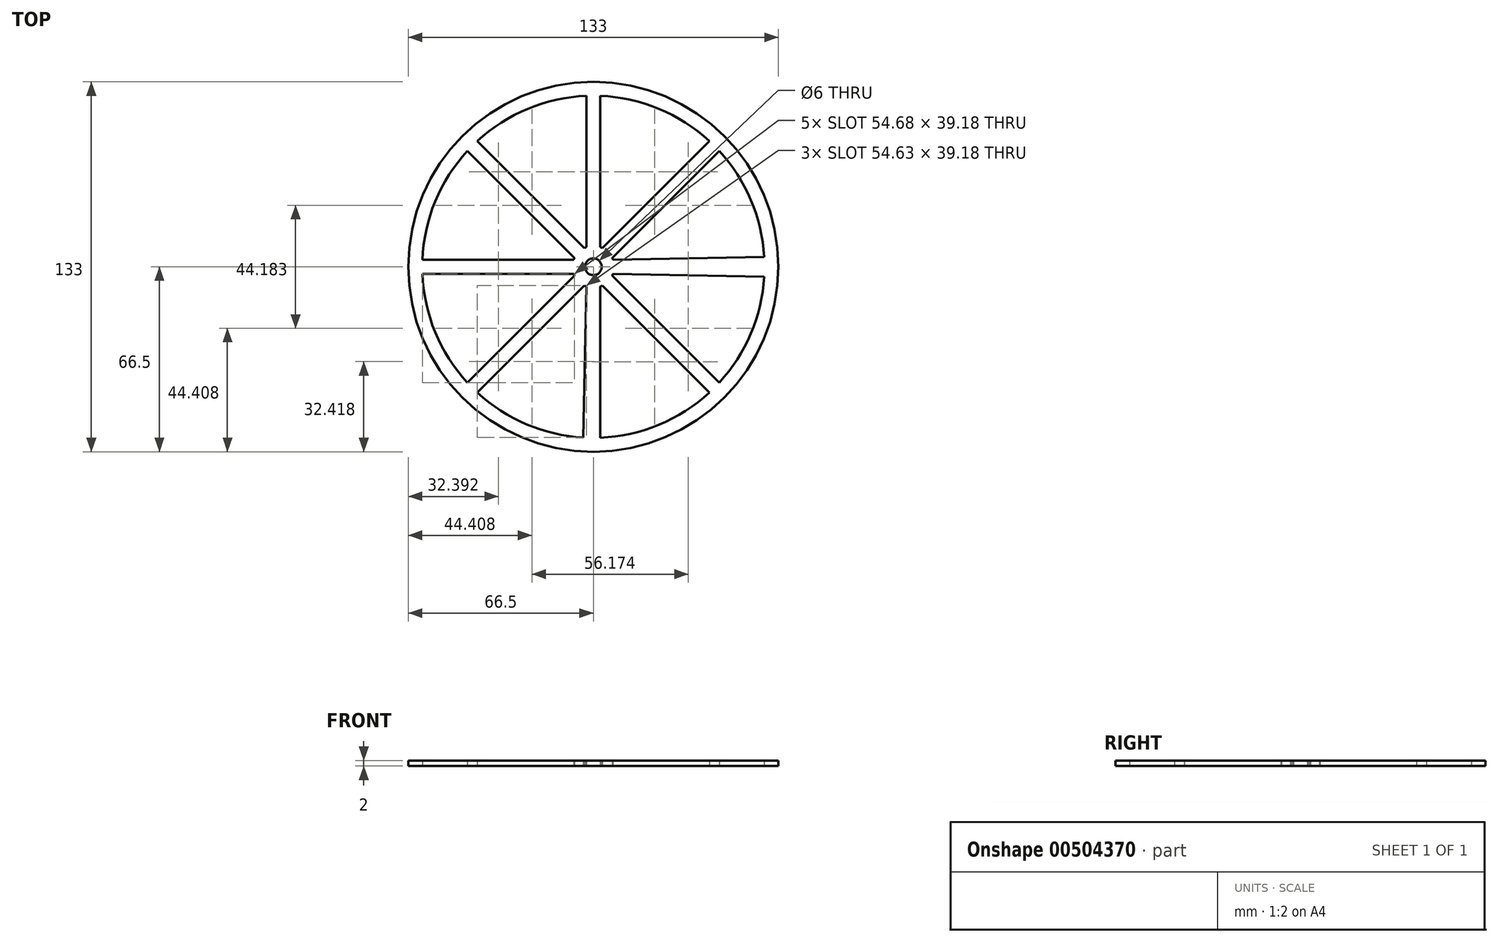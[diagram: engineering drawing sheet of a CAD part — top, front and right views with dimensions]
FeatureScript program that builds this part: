
annotation { "Feature Type Name" : "Feature", "Feature Type Description" : "" }
export const myFeature = defineFeature(function(context is Context, id is Id, definition is map)
    precondition{}
    {
        {
            var Q0;
            Q0=qCreatedBy(makeId("Top.planeOp"),FACE);
            var sketch = newSketch(context, id + "F0", { "sketchPlane" : qUnion([Q0])});
            skArc(sketch, "E0", {"start": v(-45.22, 41.68) * mm, "mid": v(-56.82, 23.54) * mm, "end": v(-61.45, 2.5) * mm});
            skCircle(sketch, "E1", {"center": v(0, 0) * mm, "radius": 66.5 * mm});
            skLineSegment(sketch, "E2", {"start": v(0, 0) * mm, "end": v(-41.68, 41.68) * mm, "construction": true});
            skLineSegment(sketch, "E3.left", {"start": v(-2.5, 61.45) * mm, "end": v(-2.5, 7.07) * mm});
            skLineSegment(sketch, "E3.right", {"start": v(2.5, 42.93) * mm, "end": v(2.5, 7.07) * mm});
            skLineSegment(sketch, "E4.bottom", {"start": v(-61.45, 2.5) * mm, "end": v(-7.07, 2.5) * mm});
            skLineSegment(sketch, "E4.top", {"start": v(-61.45, -2.5) * mm, "end": v(-7.07, -2.5) * mm});
            skLineSegment(sketch, "E5", {"start": v(-41.68, 45.22) * mm, "end": v(-3.23, 6.77) * mm});
            skLineSegment(sketch, "E6.MirrorCS", {"start": v(-45.22, 41.68) * mm, "end": v(-6.77, 3.23) * mm});
            skLineSegment(sketch, "E7.MirrorCS", {"start": v(41.68, 45.22) * mm, "end": v(3.23, 6.77) * mm});
            skArc(sketch, "E8", {"start": v(-2.5, 7.07) * mm, "mid": v(-2.87, 6.93) * mm, "end": v(-3.23, 6.77) * mm});
            skArc(sketch, "E9.trimOffspring", {"start": v(-6.77, 3.23) * mm, "mid": v(-6.93, 2.87) * mm, "end": v(-7.07, 2.5) * mm});
            skArc(sketch, "E10.trimOffspring", {"start": v(-7.07, -2.5) * mm, "mid": v(-6.93, -2.87) * mm, "end": v(-6.77, -3.23) * mm});
            skLineSegment(sketch, "E11.trimOffspring", {"start": v(-6.77, -3.23) * mm, "end": v(-45.22, -41.68) * mm});
            skArc(sketch, "E12.trimOffspring", {"start": v(-3.23, -6.77) * mm, "mid": v(-2.87, -6.93) * mm, "end": v(-2.5, -7.07) * mm});
            skLineSegment(sketch, "E13.trimOffspring", {"start": v(-3.23, -6.77) * mm, "end": v(-41.68, -45.22) * mm});
            skLineSegment(sketch, "E14.trimOffspring", {"start": v(-2.5, -7.07) * mm, "end": v(-3.58, -61.4) * mm});
            skLineSegment(sketch, "E15.trimOffspring", {"start": v(2.5, -7.07) * mm, "end": v(2.5, -61.45) * mm});
            skLineSegment(sketch, "E16.trimOffspring", {"start": v(3.23, -6.77) * mm, "end": v(41.68, -45.22) * mm});
            skArc(sketch, "E17.trimOffspring", {"start": v(2.5, -7.07) * mm, "mid": v(2.87, -6.93) * mm, "end": v(3.23, -6.77) * mm});
            skArc(sketch, "E18.trimOffspring", {"start": v(6.77, -3.23) * mm, "mid": v(6.93, -2.87) * mm, "end": v(7.07, -2.5) * mm});
            skLineSegment(sketch, "E19.trimOffspring", {"start": v(6.77, -3.23) * mm, "end": v(45.22, -41.68) * mm});
            skLineSegment(sketch, "E20.trimOffspring", {"start": v(7.07, -2.5) * mm, "end": v(61.4, -3.58) * mm});
            skArc(sketch, "E21.trimOffspring", {"start": v(7.07, 2.5) * mm, "mid": v(6.93, 2.87) * mm, "end": v(6.77, 3.23) * mm});
            skArc(sketch, "E22.trimOffspring", {"start": v(3.23, 6.77) * mm, "mid": v(2.87, 6.93) * mm, "end": v(2.5, 7.07) * mm});
            skLineSegment(sketch, "E23.trimOffspring", {"start": v(7.07, 2.5) * mm, "end": v(61.4, 3.58) * mm});
            skPoint(sketch, "E24.MirrorCS.start.orphan", {"position": v(45.22, 41.68) * mm});
            skCircle(sketch, "E25", {"center": v(0, 0) * mm, "radius": 3 * mm});
            skLineSegment(sketch, "E26.MirrorCS", {"start": v(45.22, 41.68) * mm, "end": v(6.77, 3.23) * mm});
            skArc(sketch, "E27.trimOffspring", {"start": v(41.68, 45.22) * mm, "mid": v(23.54, 56.82) * mm, "end": v(2.5, 61.45) * mm});
            skArc(sketch, "E28.trimOffspring", {"start": v(45.22, -41.68) * mm, "mid": v(56.61, -24.03) * mm, "end": v(61.4, -3.58) * mm});
            skArc(sketch, "E29.trimOffspring", {"start": v(-41.68, -45.22) * mm, "mid": v(-24.03, -56.61) * mm, "end": v(-3.58, -61.4) * mm});
            skArc(sketch, "E30.trimOffspring", {"start": v(2.5, -61.45) * mm, "mid": v(23.54, -56.82) * mm, "end": v(41.68, -45.22) * mm});
            skArc(sketch, "E31.trimOffspring", {"start": v(61.4, 3.58) * mm, "mid": v(56.61, 24.03) * mm, "end": v(45.22, 41.68) * mm});
            skArc(sketch, "E32.trimOffspring", {"start": v(-61.45, -2.5) * mm, "mid": v(-56.82, -23.54) * mm, "end": v(-45.22, -41.68) * mm});
            skLineSegment(sketch, "E33", {"start": v(2.5, 42.93) * mm, "end": v(2.5, 61.45) * mm});
            skArc(sketch, "E34.trimOffspring", {"start": v(-2.5, 61.45) * mm, "mid": v(-23.54, 56.82) * mm, "end": v(-41.68, 45.22) * mm});
            skSolve(sketch);
        }
        {
            var Q0;
            Q0=qSketchRegion(id+"F0",true);
            extrude(context, id + "F1", {"entities" : qUnion([Q0]), "depth" : 2 * mm});
        }
    });
